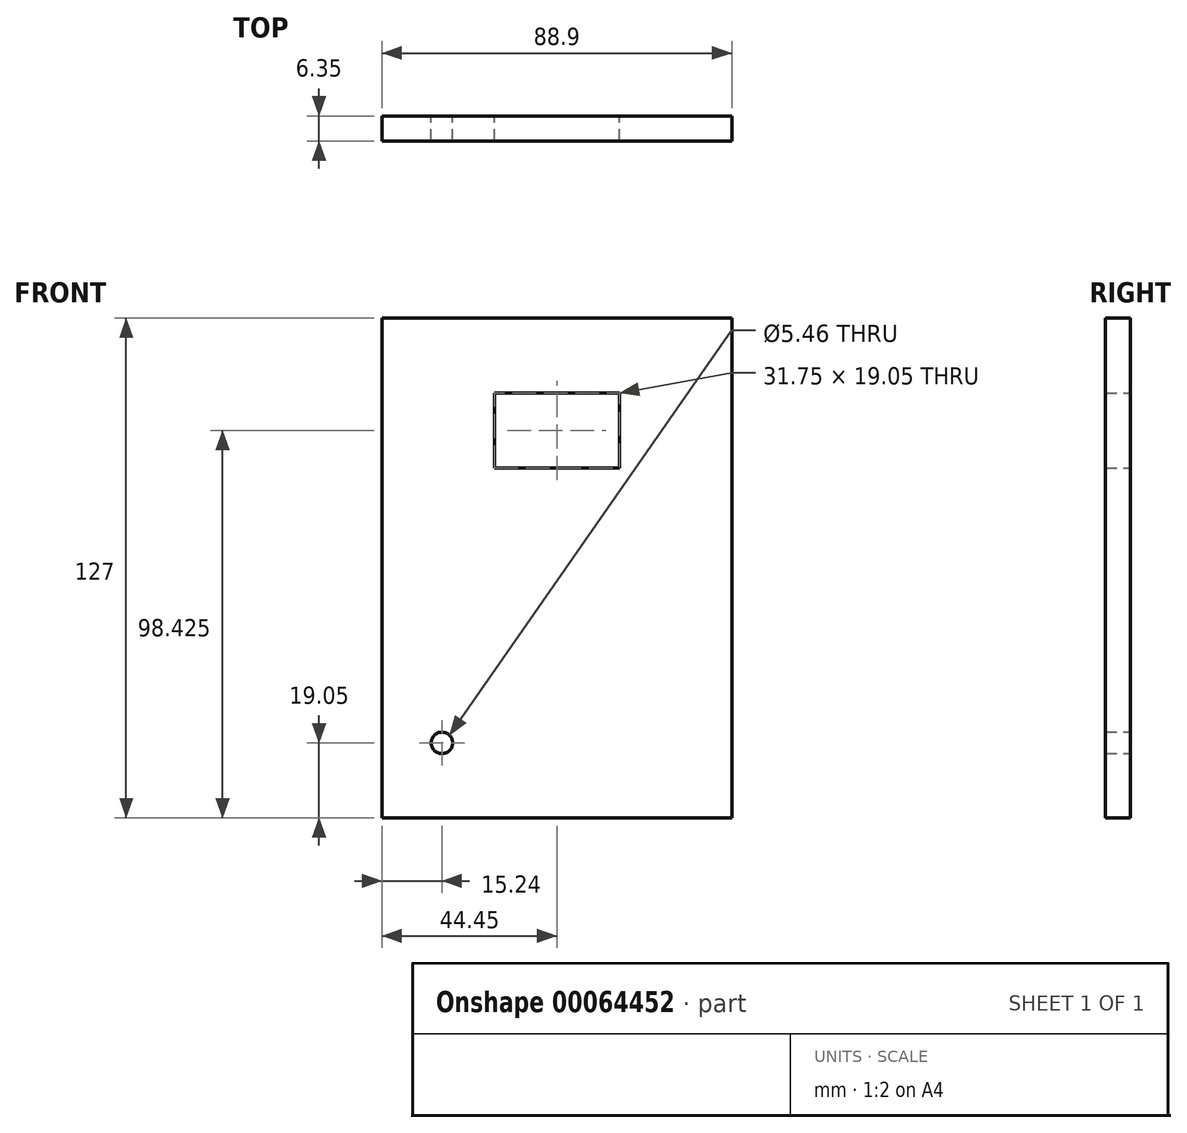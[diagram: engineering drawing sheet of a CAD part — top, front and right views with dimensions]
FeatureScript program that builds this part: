
annotation { "Feature Type Name" : "Feature", "Feature Type Description" : "" }
export const myFeature = defineFeature(function(context is Context, id is Id, definition is map)
    precondition{}
    {
        {
            var Q0;
            Q0=qCreatedBy(makeId("Front.planeOp"),FACE);
            var sketch = newSketch(context, id + "F0", { "sketchPlane" : qUnion([Q0])});
            skLineSegment(sketch, "E0.rect.bottom", {"start": v(44.45, 63.5) * mm, "end": v(-44.45, 63.5) * mm});
            skLineSegment(sketch, "E0.rect.top", {"start": v(44.45, -63.5) * mm, "end": v(-44.45, -63.5) * mm});
            skLineSegment(sketch, "E0.rect.left", {"start": v(44.45, 63.5) * mm, "end": v(44.45, -63.5) * mm});
            skLineSegment(sketch, "E0.rect.right", {"start": v(-44.45, 63.5) * mm, "end": v(-44.45, -63.5) * mm});
            skPoint(sketch, "E0.rect.middle", {"position": v(0, 0) * mm});
            skLineSegment(sketch, "E1.bottom", {"start": v(-15.87, 44.45) * mm, "end": v(15.87, 44.45) * mm});
            skLineSegment(sketch, "E1.top", {"start": v(-15.88, 25.4) * mm, "end": v(15.88, 25.4) * mm});
            skLineSegment(sketch, "E1.left", {"start": v(-15.88, 44.45) * mm, "end": v(-15.87, 25.4) * mm});
            skLineSegment(sketch, "E1.right", {"start": v(15.87, 44.45) * mm, "end": v(15.87, 25.4) * mm});
            skPoint(sketch, "E2", {"position": v(0, 63.5) * mm});
            skPoint(sketch, "E3", {"position": v(0, 44.45) * mm});
            skLineSegment(sketch, "E4", {"start": v(0, 63.5) * mm, "end": v(0, 44.45) * mm, "construction": true});
            skCircle(sketch, "E5", {"center": v(-29.21, -44.45) * mm, "radius": 2.73 * mm});
            skSolve(sketch);
        }
        {
            var Q0;
            Q0=qSketchRegion(id+"F0",true);
            extrude(context, id + "F1", {"entities" : qUnion([Q0]), "depth" : 6.35 * mm});
        }
    });
